# Revit family: Sink-Undermount-Lavatory-KOHLER-Sartorial-K-29471
name_source: partatom
category: Plumbing Fixtures
units: mm (PartAtom-declared; Revit-internal decimal feet)

## family parameters
Cut with Voids When Loaded = No
Host = Face
OmniClass Number = 23.31.13.00
OmniClass Title = Sinks
Part Type = Normal
Room Calculation Point = No
Round Connector Dimension = Use Diameter
Shared = No

## types (4) — shared parameters
ADA Compliant = Yes
Assembly Code = D2010400
CW Connection = No
Cold Water Inlet = Cold Water Inlet
Date Modified = 10/06/2022
Default Elevation = 36"
Description = Undermount Bathroom Sink
Drain Included = Yes
HW Connection = No
Height = 7 5/16"
Hot Water Inlet = Hot Water Inlet
Length = 19 15/16"
Manufacturer = Kohler Co.
Master Format 2014 = 22 41 16
Master Format 2014 Name = Residential Lavatories and Sinks
Material = Vitreous China
Product Documentation Link = https://www.us.kohler.com
Product Name = Sartorial
Product Page URL = http://www.us.kohler.com
URL = https://www.us.kohler.com
Vent Connection = No
Waste Connection = Yes
Waste Water Outlet = Waste Water Outlet
WaterSense Certified = No
Width = 15 9/16"

## per-type parameters (varying)
| type | Finish | Model | Type |
| FP1,0-White | Kohler-Vitreous_China-0-White | K-29471-FP1-0 | 1 |
| FP2,7-Black Black | Kohler-Vitreous_China-7-Black_Black | K-29471-FP2-7 | 2 |
| HD1,0-White | Kohler-Vitreous_China-0-White | K-29471-HD1-0 | 3 |
| HD2,7-Black Black | Kohler-Vitreous_China-7-Black_Black | K-29471-HD2-7 | 4 |

## geometry (parser evidence)
native form markers: Sweep x5
no freeform markers — native parametric forms only
